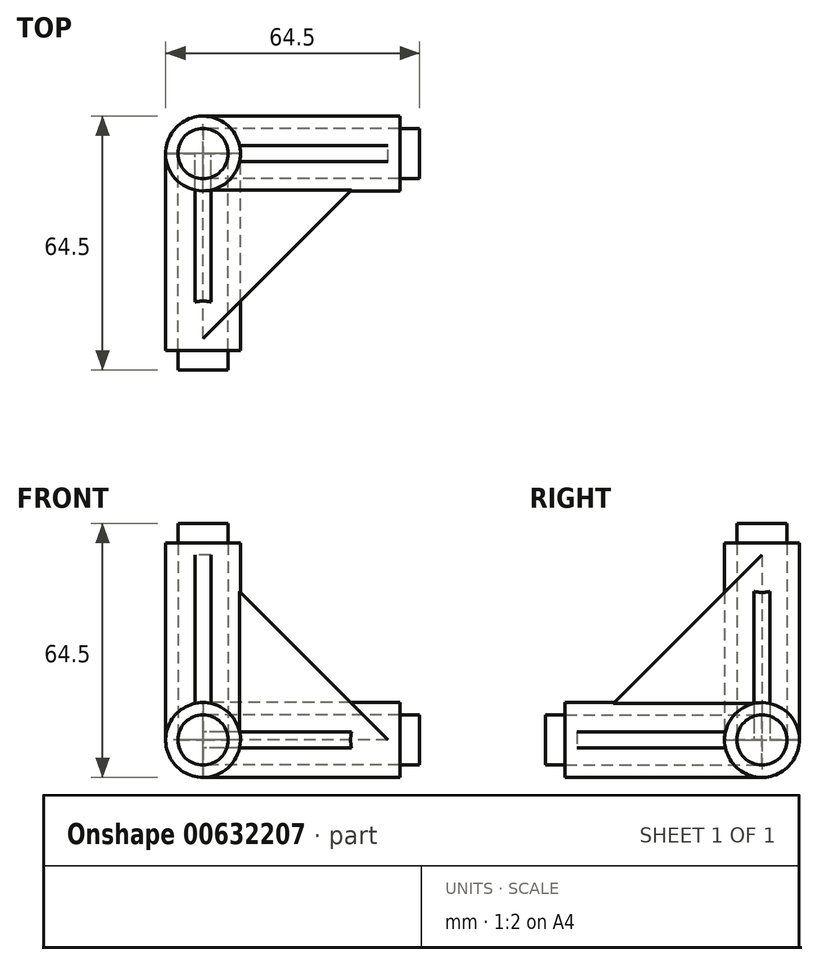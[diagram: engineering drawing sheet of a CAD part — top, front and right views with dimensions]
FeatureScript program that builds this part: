
annotation { "Feature Type Name" : "Feature", "Feature Type Description" : "" }
export const myFeature = defineFeature(function(context is Context, id is Id, definition is map)
    precondition{}
    {
        {
            assignVariable(context, id + "F0", {"name" : "PipeLength", "anyValue" : 50 * mm});
        }
        {
            var Q0;
            Q0=qCreatedBy(makeId("Front.planeOp"),FACE);
            var sketch = newSketch(context, id + "F1", { "sketchPlane" : qUnion([Q0])});
            skCircle(sketch, "E0", {"center": v(0, 0) * mm, "radius": 9.5 * mm});
            skLineSegment(sketch, "E1", {"start": v(0, 9.5) * mm, "end": v(0, -9.5) * mm});
            skLineSegment(sketch, "E2", {"start": v(0, 25.4) * mm, "end": v(0, -23.25) * mm, "construction": true});
            skCircle(sketch, "E3", {"center": v(0, 0) * mm, "radius": 6.38 * mm});
            skSolve(sketch);
        }
        {
            var Q0;
            Q0=makeQuery(id+"F1.imprint","IMPRINT",FACE,{"disambiguationData":[TD([[makeQuery(id+"F1.imprint","IMPRINT",EDGE,{"derivedFrom":sQuery(id+"F1.wireOp",EDGE,"E0")}),1.0]])]});
            var Q1;
            {var subQ0=sQuery(id+"F1.wireOp",EDGE,"E3");var subQ1=sQuery(id+"F1.wireOp",EDGE,"E1");var subQ2=makeQuery(id+"F1.imprint","INTERSECT",VERTEX,{"disambiguationData":[OD(0.0)],"derivedFrom":[subQ1,subQ0]});Q1=makeQuery(id+"F1.imprint","IMPRINT",FACE,{"disambiguationData":[TD([[makeQuery(id+"F1.imprint","IMPRINT",EDGE,{"disambiguationData":[TD([[subQ2,-1.0]])],"derivedFrom":subQ1}),-1.0]])]});}
            var Q2;
            {var subQ0=sQuery(id+"F1.wireOp",EDGE,"E3");var subQ1=sQuery(id+"F1.wireOp",EDGE,"E1");var subQ2=makeQuery(id+"F1.imprint","INTERSECT",VERTEX,{"disambiguationData":[OD(0.0)],"derivedFrom":[subQ1,subQ0]});Q2=makeQuery(id+"F1.imprint","IMPRINT",FACE,{"disambiguationData":[TD([[makeQuery(id+"F1.imprint","IMPRINT",EDGE,{"disambiguationData":[TD([[subQ2,-1.0]])],"derivedFrom":subQ1}),1.0]])]});}
            extrude(context, id + "F2", {"entities" : qUnion([Q0, Q1, Q2]), "depth" : getVariable(context, 'PipeLength'), "offsetDistance" : 25 * mm});
        }
        {
            var Q0;
            Q0=qCreatedBy(makeId("Right.planeOp"),FACE);
            var sketch = newSketch(context, id + "F3", { "sketchPlane" : qUnion([Q0])});
            skLineSegment(sketch, "E4", {"start": v(-38.5, 7) * mm, "end": v(0, 7) * mm, "construction": true});
            skLineSegment(sketch, "E5", {"start": v(0, 0) * mm, "end": v(0, 36.54) * mm, "construction": true});
            skLineSegment(sketch, "E6", {"start": v(-40, 7) * mm, "end": v(0, 47) * mm});
            skLineSegment(sketch, "E7", {"start": v(0, 47) * mm, "end": v(0, 7) * mm});
            skLineSegment(sketch, "E8", {"start": v(-40, 7) * mm, "end": v(0, 7) * mm});
            skSolve(sketch);
        }
        {
            var Q0;
            Q0 = qSketchRegion(id + "F3", true);
            extrude(context, id + "F4", {"entities" : qUnion([Q0]), "operationType" : NewBodyOperationType.ADD, "depth" : 2 * mm, "offsetDistance" : 25 * mm, "hasSecondDirection" : true, "secondDirectionOppositeDirection" : true, "secondDirectionDepth" : 2 * mm});
        }
        {
            var Q0;
            Q0=qCreatedBy(makeId("Top.planeOp"),FACE);
            var sketch = newSketch(context, id + "F5", { "sketchPlane" : qUnion([Q0])});
            skLineSegment(sketch, "E9", {"start": v(0, 0) * mm, "end": v(81.23, 0) * mm, "construction": true});
            skLineSegment(sketch, "E10", {"start": v(0, 0) * mm, "end": v(0, -92) * mm, "construction": true});
            skSolve(sketch);
        }
        {
            var Q0;
            Q0=qCreatedBy(makeId("Front.planeOp"),FACE);
            var sketch = newSketch(context, id + "F6", { "sketchPlane" : qUnion([Q0])});
            skLineSegment(sketch, "E11", {"start": v(0, 0) * mm, "end": v(0, 71.57) * mm, "construction": true});
            skSolve(sketch);
        }
        {
            var Q0;
            Q0=makeQuery(id+"F2.opExtrude","SWEPT_BODY",BODY,{"disambiguationData":[OSD([sQuery(id+"F1.wireOp",EDGE,"E0")])]});
            var Q1;
            Q1=sQuery(id+"F6.wireOp",EDGE,"E11");
            transform(context, id + "F7", {"entities" : qUnion([Q0]), "transformType" : TransformType.ROTATION, "transformAxis" : qUnion([Q1]), "angle" : 90 * degree, "makeCopy" : true});
        }
        {
            var Q0;
            Q0=makeQuery(id+"F7.opPattern","COPY",BODY,{"derivedFrom":makeQuery(id+"F2.opExtrude","SWEPT_BODY",BODY,{"disambiguationData":[OSD([sQuery(id+"F1.wireOp",EDGE,"E0")])]}),"instanceName":"1"});
            var Q1;
            Q1=sQuery(id+"F5.wireOp",EDGE,"E9");
            transform(context, id + "F8", {"entities" : qUnion([Q0]), "transformType" : TransformType.ROTATION, "transformAxis" : qUnion([Q1]), "angle" : 90 * degree, "makeCopy" : false});
        }
        {
            var Q0;
            Q0=makeQuery(id+"F2.opExtrude","SWEPT_BODY",BODY,{"disambiguationData":[OSD([sQuery(id+"F1.wireOp",EDGE,"E0")])]});
            var Q1;
            Q1=sQuery(id+"F5.wireOp",EDGE,"E9");
            transform(context, id + "F9", {"entities" : qUnion([Q0]), "transformType" : TransformType.ROTATION, "transformAxis" : qUnion([Q1]), "angle" : 90 * degree, "oppositeDirection" : true, "makeCopy" : true});
        }
        {
            var Q0;
            Q0=makeQuery(id+"F9.opPattern","COPY",BODY,{"derivedFrom":makeQuery(id+"F2.opExtrude","SWEPT_BODY",BODY,{"disambiguationData":[OSD([sQuery(id+"F1.wireOp",EDGE,"E0")])]}),"instanceName":"1"});
            var Q1;
            Q1=sQuery(id+"F6.wireOp",EDGE,"E11");
            transform(context, id + "F10", {"entities" : qUnion([Q0]), "transformType" : TransformType.ROTATION, "transformAxis" : qUnion([Q1]), "angle" : 90 * degree, "oppositeDirection" : true, "makeCopy" : false});
        }
        {
            var Q0;
            {var subQ0=sQuery(id+"F1.wireOp",EDGE,"E1");var subQ1=sQuery(id+"F1.wireOp",EDGE,"E0");var subQ2=makeQuery(id+"F1.imprint","INTERSECT",VERTEX,{"disambiguationData":[OD(0.0)],"derivedFrom":[subQ1,subQ0]});Q0=makeQuery(id+"F1.imprint","IMPRINT",FACE,{"disambiguationData":[TD([[makeQuery(id+"F1.imprint","IMPRINT",EDGE,{"disambiguationData":[TD([[subQ2,-1.0]])],"derivedFrom":subQ1}),1.0]])]});}
            var Q1;
            {var subQ0=sQuery(id+"F1.wireOp",EDGE,"E3");var subQ1=sQuery(id+"F1.wireOp",EDGE,"E1");var subQ2=makeQuery(id+"F1.imprint","INTERSECT",VERTEX,{"disambiguationData":[OD(0.0)],"derivedFrom":[subQ1,subQ0]});Q1=makeQuery(id+"F1.imprint","IMPRINT",FACE,{"disambiguationData":[TD([[makeQuery(id+"F1.imprint","IMPRINT",EDGE,{"disambiguationData":[TD([[subQ2,-1.0]])],"derivedFrom":subQ1}),-1.0]])]});}
            var Q2;
            Q2=sQuery(id+"F1.wireOp",EDGE,"E2");
            revolve(context, id + "F11", {"entities" : qUnion([Q0, Q1]), "axis" : qUnion([Q2]), "revolveType" : RevolveType.FULL});
        }
        {
            var Q0;
            {var subQ0=sQuery(id+"F1.wireOp",EDGE,"E3");var subQ1=sQuery(id+"F1.wireOp",EDGE,"E1");var subQ2=makeQuery(id+"F1.imprint","INTERSECT",VERTEX,{"disambiguationData":[OD(0.0)],"derivedFrom":[subQ1,subQ0]});Q0=makeQuery(id+"F1.imprint","IMPRINT",FACE,{"disambiguationData":[TD([[makeQuery(id+"F1.imprint","IMPRINT",EDGE,{"disambiguationData":[TD([[subQ2,-1.0]])],"derivedFrom":subQ1}),-1.0]])]});}
            var Q1;
            {var subQ0=sQuery(id+"F1.wireOp",EDGE,"E3");var subQ1=sQuery(id+"F1.wireOp",EDGE,"E1");var subQ2=makeQuery(id+"F1.imprint","INTERSECT",VERTEX,{"disambiguationData":[OD(0.0)],"derivedFrom":[subQ1,subQ0]});Q1=makeQuery(id+"F1.imprint","IMPRINT",FACE,{"disambiguationData":[TD([[makeQuery(id+"F1.imprint","IMPRINT",EDGE,{"disambiguationData":[TD([[subQ2,-1.0]])],"derivedFrom":subQ1}),1.0]])]});}
            var Q2;
            Q2=sQuery(id+"F4QjBXWZ3YFPx9k_2.wireOp",EDGE,"GEMcpwnV-hY5X-5Gvc-SFH1-QRupw2dxjbfl");
            extrude(context, id + "F12", {"entities" : qUnion([Q0, Q1]), "surfaceEntities" : qUnion([Q2]), "depth" : 55 * mm, "offsetDistance" : 25 * mm});
        }
        {
            var Q0;
            Q0=makeQuery(id+"F12.opExtrude","SWEPT_BODY",BODY,{"disambiguationData":[OSD([sQuery(id+"F1.wireOp",EDGE,"E3")])]});
            var Q1;
            Q1=sQuery(id+"F6.wireOp",EDGE,"E11");
            transform(context, id + "F13", {"entities" : qUnion([Q0]), "transformType" : TransformType.ROTATION, "transformAxis" : qUnion([Q1]), "angle" : 90 * degree, "makeCopy" : true});
        }
        {
            var Q0;
            Q0=makeQuery(id+"F12.opExtrude","SWEPT_BODY",BODY,{"disambiguationData":[OSD([sQuery(id+"F1.wireOp",EDGE,"E3")])]});
            var Q1;
            Q1=sQuery(id+"F5.wireOp",EDGE,"E9");
            transform(context, id + "F14", {"entities" : qUnion([Q0]), "transformType" : TransformType.ROTATION, "transformAxis" : qUnion([Q1]), "angle" : 90 * degree, "oppositeDirection" : true, "makeCopy" : true});
        }
        {
            var Q0;
            {var subQ0=sQuery(id+"F1.wireOp",EDGE,"E3");var subQ1=sQuery(id+"F1.wireOp",EDGE,"E1");var subQ2=makeQuery(id+"F1.imprint","INTERSECT",VERTEX,{"disambiguationData":[OD(0.0)],"derivedFrom":[subQ1,subQ0]});Q0=makeQuery(id+"F1.imprint","IMPRINT",FACE,{"disambiguationData":[TD([[makeQuery(id+"F1.imprint","IMPRINT",EDGE,{"disambiguationData":[TD([[subQ2,-1.0]])],"derivedFrom":subQ1}),-1.0]])]});}
            var Q1;
            Q1=sQuery(id+"F1.wireOp",EDGE,"E2");
            revolve(context, id + "F15", {"entities" : qUnion([Q0]), "axis" : qUnion([Q1]), "revolveType" : RevolveType.FULL});
        }
        {
            var Q0;
            Q0=makeQuery(id+"F15.opRevolve","SWEPT_BODY",BODY,{"disambiguationData":[OSD([sQuery(id+"F1.wireOp",EDGE,"E1"),sQuery(id+"F1.wireOp",EDGE,"E3")])]});
            var Q1;
            Q1=makeQuery(id+"F2.opExtrude","SWEPT_BODY",BODY,{"disambiguationData":[OSD([sQuery(id+"F1.wireOp",EDGE,"E0"),sQuery(id+"F1.wireOp",EDGE,"E3")])]});
            booleanBodies(context, id + "F16", {"operationType" : BooleanOperationType.SUBTRACTION, "tools" : qUnion([Q0]), "targets" : qUnion([Q1])});
        }
    });
